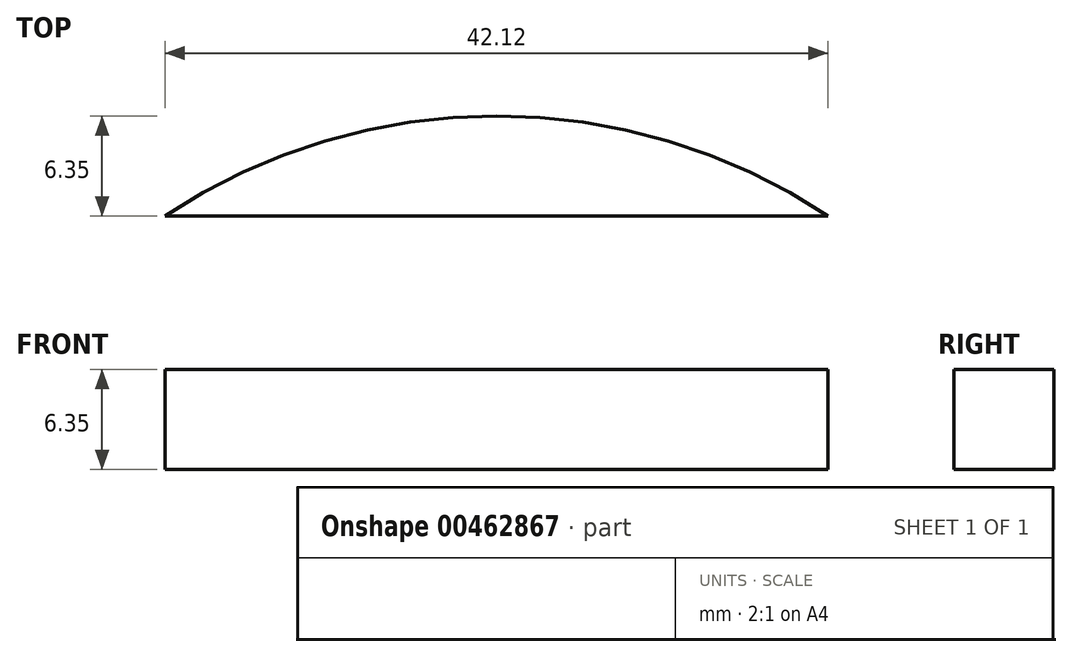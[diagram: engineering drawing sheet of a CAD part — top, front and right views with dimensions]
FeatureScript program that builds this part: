
annotation { "Feature Type Name" : "Feature", "Feature Type Description" : "" }
export const myFeature = defineFeature(function(context is Context, id is Id, definition is map)
    precondition{}
    {
        {
            var Q0;
            Q0=qCreatedBy(makeId("Top.planeOp"),FACE);
            var sketch = newSketch(context, id + "F0", { "sketchPlane" : qUnion([Q0])});
            skCircle(sketch, "E0", {"center": v(0, 0) * mm, "radius": 38.1 * mm});
            skLineSegment(sketch, "E1", {"start": v(-21.06, 31.75) * mm, "end": v(21.06, 31.75) * mm});
            skSolve(sketch);
        }
        {
            var Q0;
            {var subQ0=sQuery(id+"F0.wireOp",EDGE,"E1");Q0=makeQuery(id+"F0.imprint","IMPRINT",FACE,{"disambiguationData":[TD([[makeQuery(id+"F0.imprint","IMPRINT",EDGE,{"derivedFrom":subQ0}),1.0]])]});}
            extrude(context, id + "F1", {"entities" : qUnion([Q0]), "depth" : 6.35 * mm});
        }
    });
